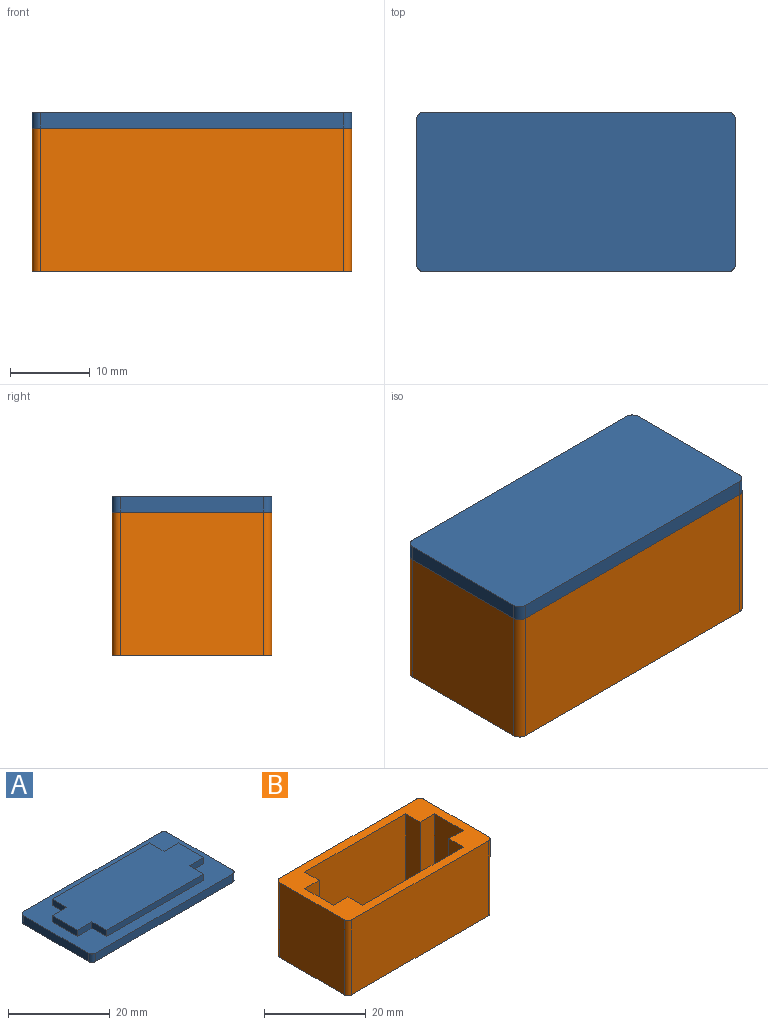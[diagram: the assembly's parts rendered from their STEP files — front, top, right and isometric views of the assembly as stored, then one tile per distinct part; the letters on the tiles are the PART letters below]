
ASSEMBLY  parts=2 mates=1
PART A: 23 faces, bbox 40x20x3.5 mm
  f0: plane 7x1.5mm, normal (-1,0,0), area 10.5mm2, adj f4,f9,f16,f22
  f1: plane 27x1.5mm, normal (0,-1,0), area 40.5mm2, adj f4,f9,f19,f21
  f2: plane 7x1.5mm, normal (1,0,0), area 10.5mm2, adj f4,f9,f18,f20
  f3: plane 27x1.5mm, normal (0,1,0), area 40.5mm2, adj f4,f9,f15,f17
  f4: plane 35x15mm, normal (0,0,1), area 461mm2, adj f0,f1,f2,f3,f15,f16,f17,f18
  f5: plane 18x2mm, normal (-1,0,0), area 36mm2, adj f9,f10,f11,f14
  f6: plane 38x2mm, normal (0,-1,0), area 76mm2, adj f9,f10,f11,f12
  f7: plane 18x2mm, normal (1,0,0), area 36mm2, adj f9,f10,f12,f13
  f8: plane 38x2mm, normal (0,1,0), area 76mm2, adj f9,f10,f13,f14
  f9: plane 40x20mm, normal (0,0,1), area 338.1mm2, adj f0,f1,f2,f3,f5,f6,f7,f8
  f10: plane 40x20mm, normal (0,0,-1), area 799.1mm2, adj f5,f6,f7,f8,f11,f12,f13,f14
  f11: cylinder r=1mm len=2mm, axis (0,0,-1), area 3.1mm2, adj f5,f6,f9,f10
  f12: cylinder r=1mm len=2mm, axis (0,0,1), area 3.1mm2, adj f6,f7,f9,f10
  f13: cylinder r=1mm len=2mm, axis (0,0,-1), area 3.1mm2, adj f7,f8,f9,f10
  f14: cylinder r=1mm len=2mm, axis (0,0,1), area 3.1mm2, adj f5,f8,f9,f10
  f15: plane 4x1.5mm, normal (-1,0,0), area 6mm2, adj f3,f4,f9,f16
  f16: plane 4x1.5mm, normal (0,1,0), area 6mm2, adj f0,f4,f9,f15
  f17: plane 4x1.5mm, normal (1,0,0), area 6mm2, adj f3,f4,f9,f18
  f18: plane 4x1.5mm, normal (0,1,0), area 6mm2, adj f2,f4,f9,f17
  f19: plane 4x1.5mm, normal (1,0,0), area 6mm2, adj f1,f4,f9,f20
  f20: plane 4x1.5mm, normal (0,-1,0), area 6mm2, adj f2,f4,f9,f19
  f21: plane 4x1.5mm, normal (-1,0,0), area 6mm2, adj f1,f4,f9,f22
  f22: plane 4x1.5mm, normal (0,-1,0), area 6mm2, adj f0,f4,f9,f21
PART B: 36 faces, bbox 40x20x18 mm
  f0: plane 36x16mm, normal (0,0,1), area 407.5mm2, adj f2,f3,f4,f5,f11,f12,f13,f14
  f1: plane 40x20mm, normal (0,0,-1), area 742mm2, adj f6,f7,f8,f9,f19,f20,f21,f22
  f2: plane 28x17mm, normal (0,1,0), area 431mm2, adj f0,f10,f15,f17,f31,f32,f34,f35
  f3: plane 17x8mm, normal (-1,0,0), area 136mm2, adj f0,f10,f14,f16
  f4: plane 17x8mm, normal (1,0,0), area 136mm2, adj f0,f10,f12,f18
  f5: plane 28x17mm, normal (0,-1,0), area 476mm2, adj f0,f10,f11,f13
  f6: plane 18x18mm, normal (-1,0,0), area 324mm2, adj f1,f10,f27,f30
  f7: plane 38x18mm, normal (0,-1,0), area 684mm2, adj f1,f10,f27,f28
  f8: plane 18x18mm, normal (1,0,0), area 324mm2, adj f1,f10,f28,f29
  f9: plane 38x18mm, normal (0,1,0), area 684mm2, adj f1,f10,f29,f30
  f10: plane 40x20mm, normal (0,0,1), area 287.1mm2, adj f2,f3,f4,f5,f6,f7,f8,f9
  f11: plane 17x4mm, normal (1,0,0), area 68mm2, adj f0,f5,f10,f12
  f12: plane 17x4mm, normal (0,-1,0), area 68mm2, adj f0,f4,f10,f11
  f13: plane 17x4mm, normal (-1,0,0), area 68mm2, adj f0,f5,f10,f14
  f14: plane 17x4mm, normal (0,-1,0), area 68mm2, adj f0,f3,f10,f13
  f15: plane 17x4mm, normal (-1,0,0), area 68mm2, adj f0,f2,f10,f16
  f16: plane 17x4mm, normal (0,1,0), area 68mm2, adj f0,f3,f10,f15
  f17: plane 17x4mm, normal (1,0,0), area 68mm2, adj f0,f2,f10,f18
  f18: plane 17x4mm, normal (0,1,0), area 68mm2, adj f0,f4,f10,f17
  f19: plane 4x1mm, normal (0.71,0,0.71), area 5.7mm2, adj f0,f1,f20,f21
  f20: cone r=3mm half-angle=45deg, axis (0,0,1), area 11.1mm2, adj f0,f1,f19,f22
  f21: cone r=3mm half-angle=45deg, axis (0,0,1), area 11.1mm2, adj f0,f1,f19,f22
  f22: plane 4x1mm, normal (-0.71,0,0.71), area 5.7mm2, adj f0,f1,f20,f21
  f23: plane 4x1mm, normal (0.71,0,0.71), area 5.7mm2, adj f0,f1,f24,f25
  f24: cone r=1.5mm half-angle=45deg, axis (0,0,1), area 11.1mm2, adj f0,f1,f23,f26
  f25: cone r=3mm half-angle=45deg, axis (0,0,1), area 11.1mm2, adj f0,f1,f23,f26
  f26: plane 4x1mm, normal (-0.71,0,0.71), area 5.7mm2, adj f0,f1,f24,f25
  f27: cylinder r=1mm len=18mm, axis (0,0,-1), area 28.3mm2, adj f1,f6,f7,f10
  f28: cylinder r=1mm len=18mm, axis (0,0,1), area 28.3mm2, adj f1,f7,f8,f10
  f29: cylinder r=1mm len=18mm, axis (0,0,-1), area 28.3mm2, adj f1,f8,f9,f10
  f30: cylinder r=1mm len=18mm, axis (0,0,1), area 28.3mm2, adj f1,f6,f9,f10
  f31: plane 3x0.5mm, normal (1,0,0), area 1.2mm2, adj f2,f33,f34,f35
  f32: plane 3x0.5mm, normal (-1,0,0), area 1.2mm2, adj f2,f33,f34,f35
  f33: plane 15x2mm, normal (0,1,0), area 30mm2, adj f31,f32,f34,f35
  f34: plane 15x0.5mm, normal (0,0.71,-0.71), area 10.6mm2, adj f2,f31,f32,f33
  f35: plane 15x0.5mm, normal (0,0.71,0.71), area 10.6mm2, adj f2,f31,f32,f33
PLACE A rot(axis=(1,0,0),180deg) t=(-60,81.36,20)mm
PLACE B at identity fixed
MATE slider A.f14 <-> B.f27  axis (0,0,-1) through (-57.33,31.68,18)mm
